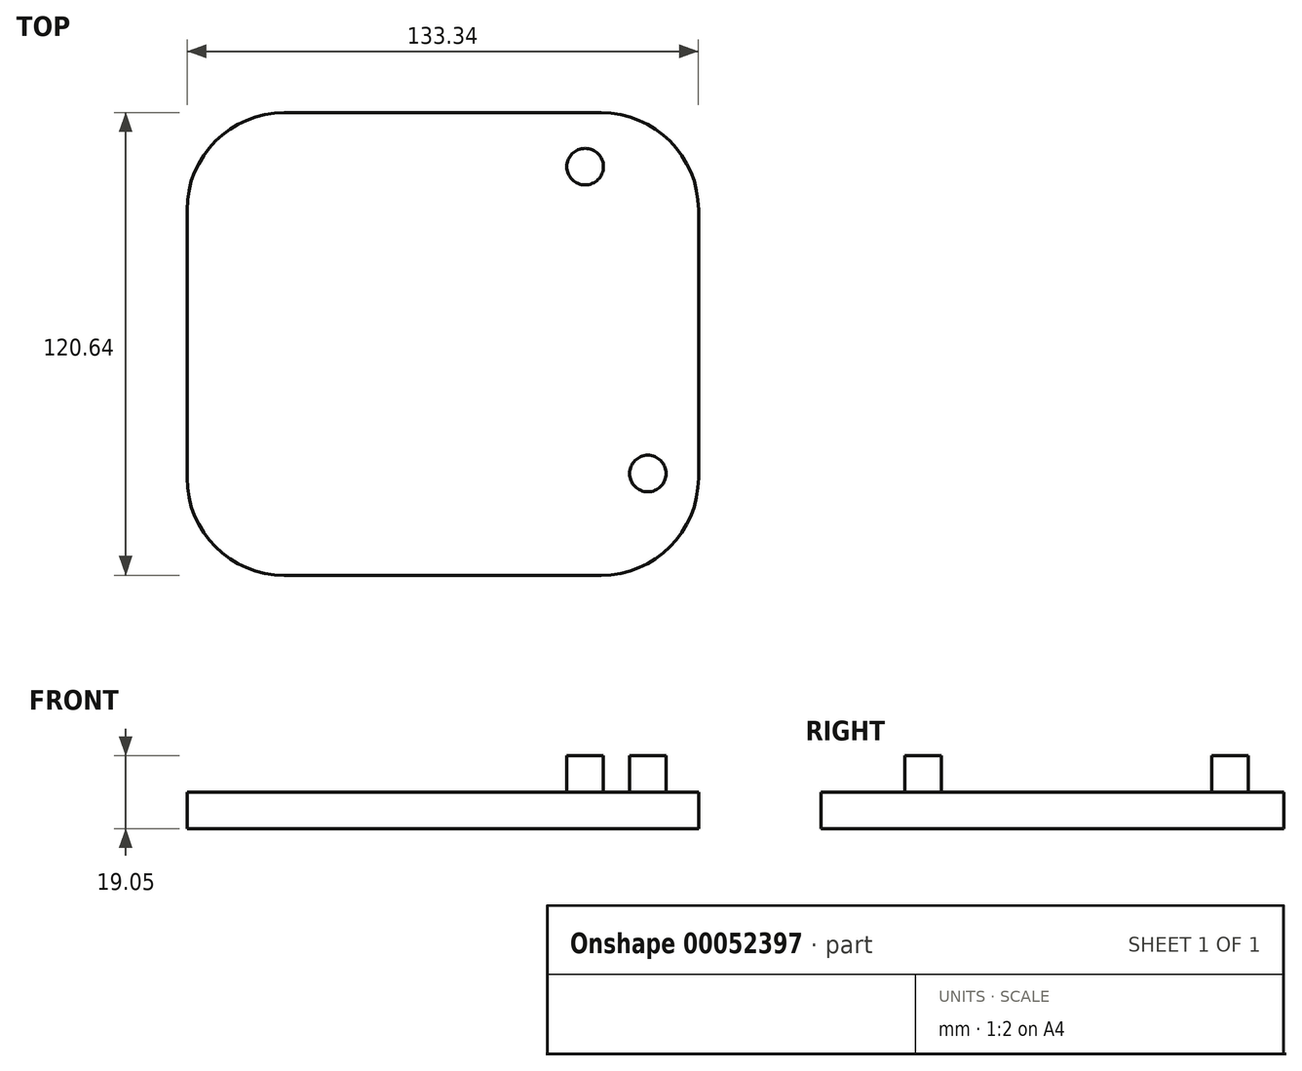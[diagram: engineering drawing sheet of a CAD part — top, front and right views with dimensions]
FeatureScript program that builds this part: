
annotation { "Feature Type Name" : "Feature", "Feature Type Description" : "" }
export const myFeature = defineFeature(function(context is Context, id is Id, definition is map)
    precondition{}
    {
        {
            var Q0;
            Q0=qCreatedBy(makeId("Top.planeOp"),FACE);
            var sketch = newSketch(context, id + "F0", { "sketchPlane" : qUnion([Q0])});
            skLineSegment(sketch, "E0.rect.bottom", {"start": v(66.68, 60.33) * mm, "end": v(-66.68, 60.33) * mm});
            skLineSegment(sketch, "E0.rect.top", {"start": v(66.68, -60.33) * mm, "end": v(-66.68, -60.33) * mm});
            skLineSegment(sketch, "E0.rect.left", {"start": v(66.68, 60.33) * mm, "end": v(66.68, -60.33) * mm});
            skLineSegment(sketch, "E0.rect.right", {"start": v(-66.68, 60.33) * mm, "end": v(-66.68, -60.33) * mm});
            skPoint(sketch, "E0.rect.middle", {"position": v(0, 0) * mm});
            skSolve(sketch);
        }
        {
            var Q0;
            Q0=makeQuery(id+"F0.imprint","IMPRINT",FACE,{"disambiguationData":[TD([[makeQuery(id+"F0.imprint","IMPRINT",EDGE,{"derivedFrom":sQuery(id+"F0.wireOp",EDGE,"E0.rect.bottom")}),1.0]])]});
            extrude(context, id + "F1", {"entities" : qUnion([Q0]), "depth" : 19.05 * mm});
        }
        {
            var Q0;
            Q0=makeQuery(id+"F1.opExtrude","CAP_FACE",FACE,{"disambiguationData":[OSD([sQuery(id+"F0.wireOp",EDGE,"E0.rect.bottom"),sQuery(id+"F0.wireOp",EDGE,"E0.rect.top"),sQuery(id+"F0.wireOp",EDGE,"E0.rect.left"),sQuery(id+"F0.wireOp",EDGE,"E0.rect.right")])],"isStart":false});
            var sketch = newSketch(context, id + "F2", { "sketchPlane" : qUnion([Q0])});
            skCircle(sketch, "E1", {"center": v(-37.12, 46.23) * mm, "radius": 4.76 * mm});
            skCircle(sketch, "E2", {"center": v(-53.47, -33.77) * mm, "radius": 4.76 * mm});
            skLineSegment(sketch, "E3.top", {"start": v(-47.75, 35.9) * mm, "end": v(47.75, 35.9) * mm, "construction": true});
            skLineSegment(sketch, "E3.left", {"start": v(-47.75, -60.61) * mm, "end": v(-47.75, 35.9) * mm, "construction": true});
            skLineSegment(sketch, "E3.bottom", {"start": v(-47.75, -60.61) * mm, "end": v(47.75, -60.61) * mm, "construction": true});
            skLineSegment(sketch, "E3.right", {"start": v(47.75, -60.61) * mm, "end": v(47.75, 35.9) * mm, "construction": true});
            skLineSegment(sketch, "E4", {"start": v(0, 50.11) * mm, "end": v(0, -44.44) * mm, "construction": true});
            skCircle(sketch, "E5.MirrorC", {"center": v(53.47, -33.77) * mm, "radius": 4.76 * mm});
            skCircle(sketch, "E6.MirrorC", {"center": v(37.12, 46.23) * mm, "radius": 4.76 * mm});
            skSolve(sketch);
        }
        {
            var Q0;
            Q0=makeQuery(id+"F2.imprint","IMPRINT",FACE,{"disambiguationData":[TD([[makeQuery(id+"F2.imprint","IMPRINT",EDGE,{"derivedFrom":sQuery(id+"F2.wireOp",EDGE,"E1")}),1.0]])]});
            var Q1;
            Q1=makeQuery(id+"F2.imprint","IMPRINT",FACE,{"disambiguationData":[TD([[makeQuery(id+"F2.imprint","IMPRINT",EDGE,{"derivedFrom":sQuery(id+"F2.wireOp",EDGE,"E2")}),1.0]])]});
            var Q2;
            Q2=makeQuery(id+"F2.imprint","IMPRINT",FACE,{"disambiguationData":[TD([[makeQuery(id+"F2.imprint","IMPRINT",EDGE,{"derivedFrom":sQuery(id+"F2.wireOp",EDGE,"E6.MirrorC")}),-1.0]])]});
            var Q3;
            Q3=makeQuery(id+"F2.imprint","IMPRINT",FACE,{"disambiguationData":[TD([[makeQuery(id+"F2.imprint","IMPRINT",EDGE,{"derivedFrom":sQuery(id+"F2.wireOp",EDGE,"E5.MirrorC")}),-1.0]])]});
            var Q4;
            Q4=sQuery(id+"F2.wireOp",EDGE,"E1");
            var Q5;
            Q5=sQuery(id+"F2.wireOp",EDGE,"E2");
            extrude(context, id + "F3", {"entities" : qUnion([Q0, Q1, Q2, Q3]), "operationType" : NewBodyOperationType.REMOVE, "surfaceEntities" : qUnion([Q4, Q5]), "oppositeDirection" : true, "depth" : 9.52 * mm});
        }
        {
            var Q0;
            Q0=makeQuery(id+"F1.opExtrude","SWEPT_EDGE",EDGE,{"disambiguationData":[OSD([sQuery(id+"F0.wireOp",EDGE,"E0.rect.bottom"),sQuery(id+"F0.wireOp",EDGE,"E0.rect.left")])]});
            var Q1;
            Q1=makeQuery(id+"F1.opExtrude","SWEPT_EDGE",EDGE,{"disambiguationData":[OSD([sQuery(id+"F0.wireOp",EDGE,"E0.rect.top"),sQuery(id+"F0.wireOp",EDGE,"E0.rect.left")])]});
            var Q2;
            Q2=makeQuery(id+"F1.opExtrude","SWEPT_EDGE",EDGE,{"disambiguationData":[OSD([sQuery(id+"F0.wireOp",EDGE,"E0.rect.top"),sQuery(id+"F0.wireOp",EDGE,"E0.rect.right")])]});
            var Q3;
            Q3=makeQuery(id+"F1.opExtrude","SWEPT_EDGE",EDGE,{"disambiguationData":[OSD([sQuery(id+"F0.wireOp",EDGE,"E0.rect.bottom"),sQuery(id+"F0.wireOp",EDGE,"E0.rect.right")])]});
            fillet(context, id + "F4", {"entities" : qUnion([Q0, Q1, Q2, Q3]), "radius" : 25.4 * mm, "tangentPropagation" : true, "allowEdgeOverflow" : false});
        }
    });
